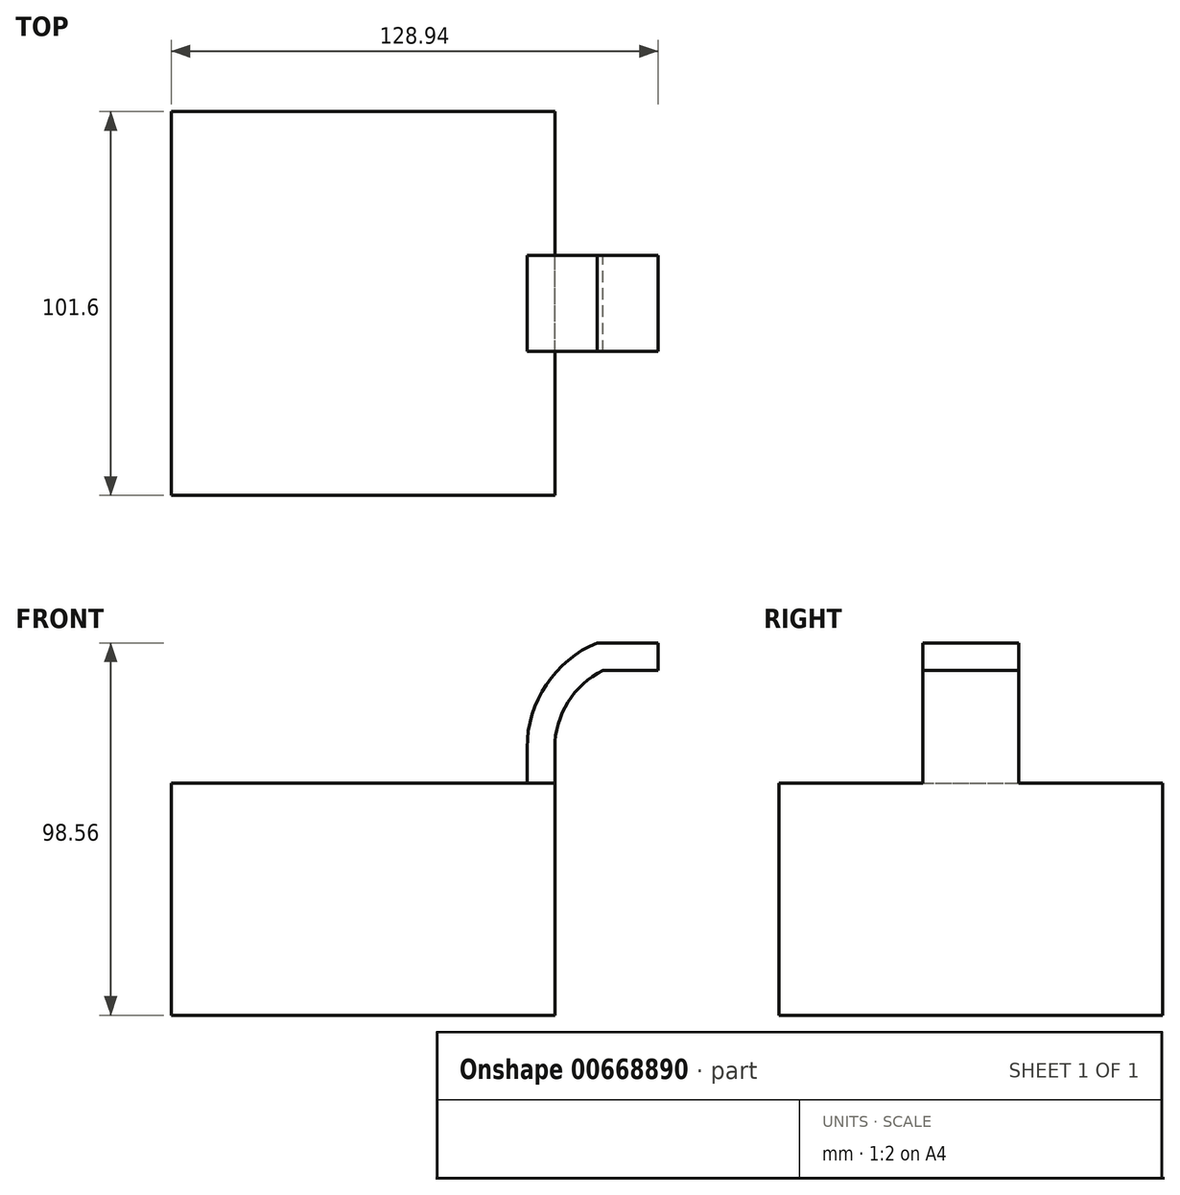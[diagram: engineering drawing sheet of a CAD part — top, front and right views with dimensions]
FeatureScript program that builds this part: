
annotation { "Feature Type Name" : "Feature", "Feature Type Description" : "" }
export const myFeature = defineFeature(function(context is Context, id is Id, definition is map)
    precondition{}
    {
        {
            var Q0;
            Q0=qCreatedBy(makeId("Front.planeOp"),FACE);
            var sketch = newSketch(context, id + "F0", { "sketchPlane" : qUnion([Q0])});
            skLineSegment(sketch, "E0.bottom", {"start": v(50.8, -30.71) * mm, "end": v(-50.8, -30.71) * mm});
            skLineSegment(sketch, "E0.top", {"start": v(50.8, 30.71) * mm, "end": v(-50.8, 30.71) * mm});
            skLineSegment(sketch, "E0.left", {"start": v(50.8, -30.71) * mm, "end": v(50.8, 30.71) * mm});
            skLineSegment(sketch, "E0.right", {"start": v(-50.8, -30.71) * mm, "end": v(-50.8, 30.71) * mm});
            skPoint(sketch, "E0.middle", {"position": v(0, 0) * mm});
            skLineSegment(sketch, "E1.bottom", {"start": v(117.03, 51.28) * mm, "end": v(78.14, 51.28) * mm});
            skLineSegment(sketch, "E1.top", {"start": v(117.03, 89.9) * mm, "end": v(78.14, 89.9) * mm});
            skLineSegment(sketch, "E1.left", {"start": v(117.03, 51.28) * mm, "end": v(117.03, 89.9) * mm});
            skLineSegment(sketch, "E1.right", {"start": v(78.14, 51.28) * mm, "end": v(78.14, 89.9) * mm});
            skPoint(sketch, "E1.middle", {"position": v(97.59, 70.58) * mm});
            skLineSegment(sketch, "E2", {"start": v(50.8, 30.71) * mm, "end": v(50.8, 40.08) * mm});
            skArc(sketch, "E3", {"start": v(50.8, 40.08) * mm, "mid": v(54.26, 52.13) * mm, "end": v(63.59, 60.51) * mm});
            skLineSegment(sketch, "E4", {"start": v(63.59, 60.51) * mm, "end": v(100.4, 60.51) * mm});
            skLineSegment(sketch, "E5.0", {"start": v(62.02, 67.85) * mm, "end": v(100.4, 67.85) * mm});
            skArc(sketch, "E5.1", {"start": v(43.46, 40.08) * mm, "mid": v(48.53, 56.78) * mm, "end": v(62.02, 67.85) * mm});
            skLineSegment(sketch, "E5.2", {"start": v(43.46, 30.71) * mm, "end": v(43.46, 40.08) * mm});
            skLineSegment(sketch, "E6", {"start": v(100.4, 51.28) * mm, "end": v(100.4, 89.9) * mm});
            skFitSpline(sketch, "E7", {"points": [v(-50.8, 30.71) * mm, v(62.02, 67.85) * mm], "startDerivative": vector(152.4, 0) * mm, "endDerivative": vector(186.07, 0.2) * mm});
            skSolve(sketch);
        }
        {
            var Q0;
            Q0=makeQuery(id+"F0.imprint","IMPRINT",FACE,{"disambiguationData":[TD([[makeQuery(id+"F0.imprint","IMPRINT",EDGE,{"derivedFrom":sQuery(id+"F0.wireOp",EDGE,"E0.bottom")}),-1.0]])]});
            extrude(context, id + "F1", {"entities" : qUnion([Q0]), "endBound" : BoundingType.SYMMETRIC, "depth" : 101.6 * mm, "offsetDistance" : 25.4 * mm});
        }
        {
            var Q0;
            Q0=makeQuery(id+"F0.imprint","IMPRINT",FACE,{"disambiguationData":[TD([[makeQuery(id+"F0.imprint","IMPRINT",EDGE,{"derivedFrom":sQuery(id+"F0.wireOp",EDGE,"E5.1")}),1.0]])]});
            extrude(context, id + "F2", {"entities" : qUnion([Q0]), "operationType" : NewBodyOperationType.ADD, "endBound" : BoundingType.SYMMETRIC, "depth" : 25.4 * mm, "offsetDistance" : 25.4 * mm});
        }
    });
